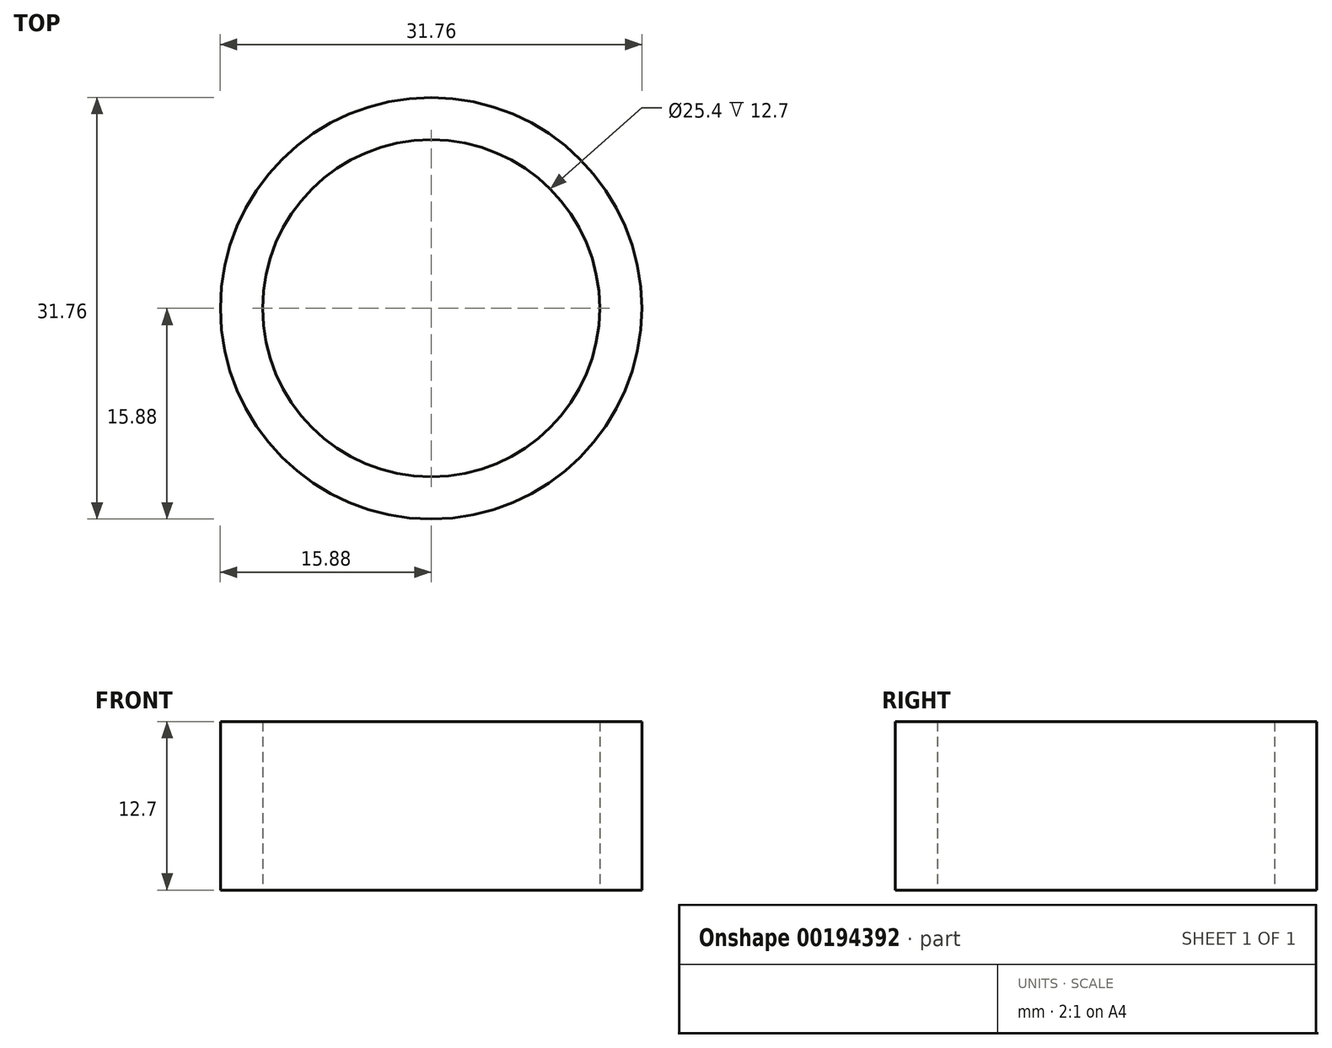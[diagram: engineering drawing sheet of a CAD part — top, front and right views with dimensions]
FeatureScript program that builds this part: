
annotation { "Feature Type Name" : "Feature", "Feature Type Description" : "" }
export const myFeature = defineFeature(function(context is Context, id is Id, definition is map)
    precondition{}
    {
        {
            var Q0;
            Q0=qCreatedBy(makeId("Top.planeOp"),FACE);
            var sketch = newSketch(context, id + "F0", { "sketchPlane" : qUnion([Q0])});
            skCircle(sketch, "E0", {"center": v(0, 0) * mm, "radius": 12.7 * mm});
            skCircle(sketch, "E1", {"center": v(0, 0) * mm, "radius": 15.88 * mm});
            skSolve(sketch);
        }
        {
            var Q0;
            Q0=makeQuery(id+"F0.imprint","IMPRINT",FACE,{"disambiguationData":[TD([[makeQuery(id+"F0.imprint","IMPRINT",EDGE,{"derivedFrom":sQuery(id+"F0.wireOp",EDGE,"E0")}),-1.0]])]});
            extrude(context, id + "F1", {"entities" : qUnion([Q0]), "depth" : 12.7 * mm});
        }
    });
